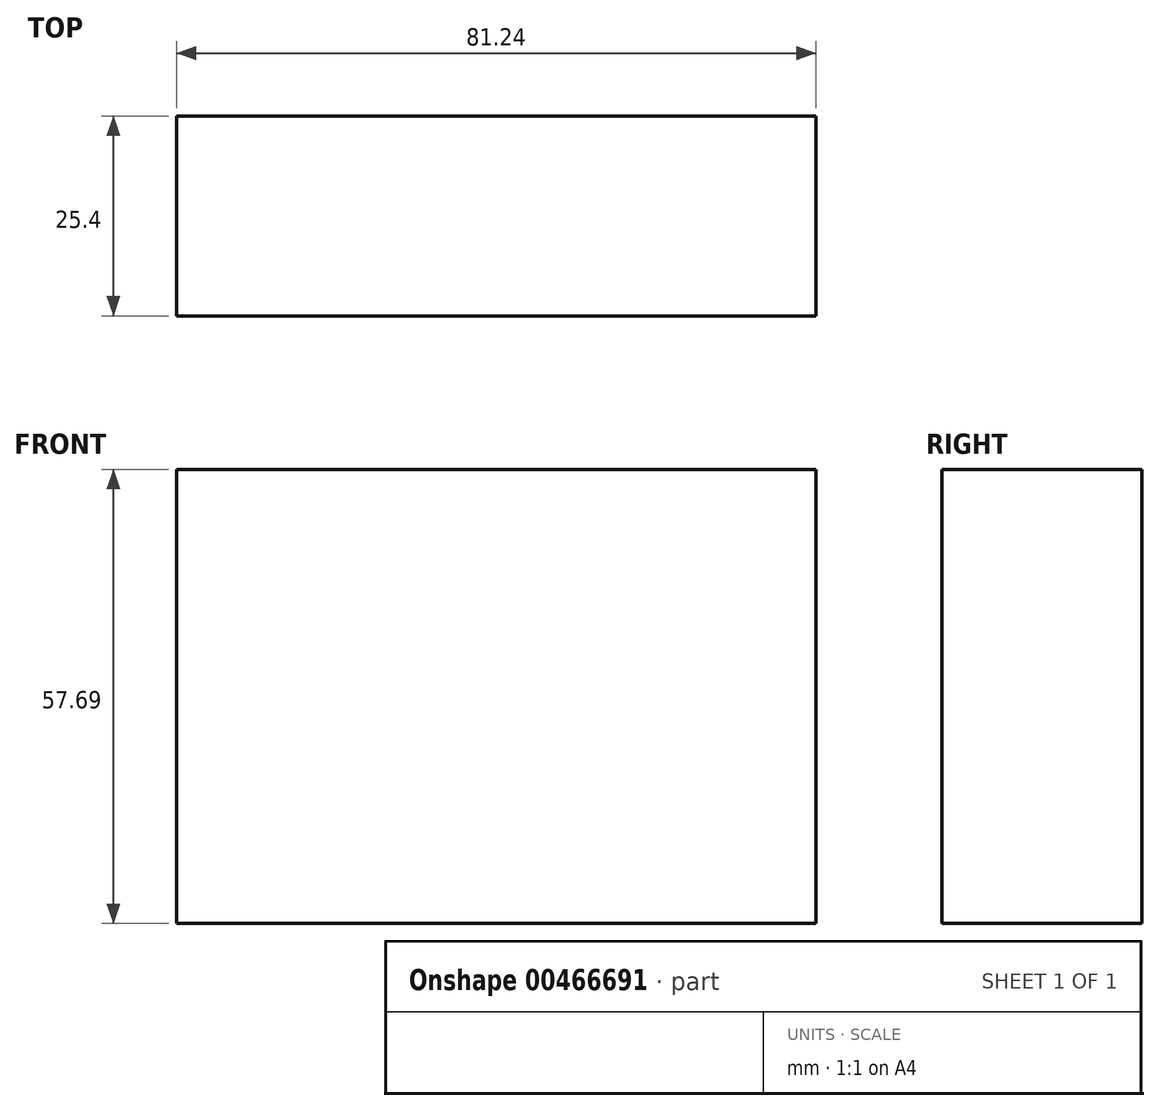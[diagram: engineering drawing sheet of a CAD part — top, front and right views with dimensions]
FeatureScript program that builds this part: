
annotation { "Feature Type Name" : "Feature", "Feature Type Description" : "" }
export const myFeature = defineFeature(function(context is Context, id is Id, definition is map)
    precondition{}
    {
        {
            var Q0;
            Q0=qCreatedBy(makeId("Front.planeOp"),FACE);
            var sketch = newSketch(context, id + "F0", { "sketchPlane" : qUnion([Q0])});
            skLineSegment(sketch, "E0.bottom", {"start": v(-49.21, 40.84) * mm, "end": v(31.64, 40.84) * mm});
            skLineSegment(sketch, "E0.top", {"start": v(-49.21, -17.24) * mm, "end": v(31.64, -17.24) * mm});
            skLineSegment(sketch, "E0.left", {"start": v(-49.21, 40.84) * mm, "end": v(-49.21, -17.24) * mm});
            skLineSegment(sketch, "E0.right", {"start": v(31.64, 40.84) * mm, "end": v(31.64, -17.24) * mm});
            skSolve(sketch);
        }
        {
            var Q0;
            Q0=sQuery(id+"F0.wireOp",EDGE,"E0.bottom");
            var Q1;
            Q1=sQuery(id+"F0.wireOp",EDGE,"E0.left");
            var Q2;
            Q2=sQuery(id+"F0.wireOp",EDGE,"E0.right");
            var Q3;
            Q3=sQuery(id+"F0.wireOp",EDGE,"E0.top");
            extrude(context, id + "F1", {"bodyType" : ToolBodyType.SURFACE, "surfaceEntities" : qUnion([Q0, Q1, Q2, Q3]), "depth" : 25.4 * mm});
        }
        {
            var Q0;
            Q0=qCreatedBy(makeId("Front.planeOp"),FACE);
            var sketch = newSketch(context, id + "F2", { "sketchPlane" : qUnion([Q0])});
            skLineSegment(sketch, "E1.bottom", {"start": v(-15.7, 19.72) * mm, "end": v(-96.94, 19.72) * mm});
            skLineSegment(sketch, "E1.top", {"start": v(-15.7, -37.97) * mm, "end": v(-96.94, -37.97) * mm});
            skLineSegment(sketch, "E1.left", {"start": v(-15.7, 19.72) * mm, "end": v(-15.7, -37.97) * mm});
            skLineSegment(sketch, "E1.right", {"start": v(-96.94, 19.72) * mm, "end": v(-96.94, -37.97) * mm});
            skSolve(sketch);
        }
        {
            var Q0;
            Q0=makeQuery(id+"F2.imprint","IMPRINT",FACE,{"disambiguationData":[TD([[makeQuery(id+"F2.imprint","IMPRINT",EDGE,{"derivedFrom":sQuery(id+"F2.wireOp",EDGE,"E1.bottom")}),1.0]])]});
            extrude(context, id + "F3", {"entities" : qUnion([Q0]), "depth" : 25.4 * mm});
        }
    });
